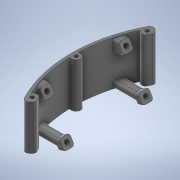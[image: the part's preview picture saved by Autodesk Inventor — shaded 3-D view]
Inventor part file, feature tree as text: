
AUTODESK INVENTOR PART (.ipt)
format: ipt  version: 2020 (Build 240168000, 168)  size: 1,327,616 bytes
history: native  units: mm
features: projected_geometry x30, extrude x17, sketch x12, other x9, fillet x1
ambient origin geometry x8: Origin, YZ Plane, XZ Plane, XY Plane, X Axis, Y Axis, Z Axis, Center Point
bodies: Body1 (feature_tree)
feature tree (69):
  other  "Твердое тело1"
  extrude  "outer"  TaperAngle=45.0deg  [1 undecoded]
  extrude  "inner"  Depth=7.0mm
  sketch  "Эскиз3"
  extrude  "Выдавливание3"  Depth=20.0mm
  extrude  "Выдавливание4"  Depth=7.0mm
  sketch  "Эскиз4"
  extrude  "Выдавливание5"  Depth=3.2mm
  extrude  "Выдавливание6"  Depth=59.0mm
  sketch  "Эскиз5"
  extrude  "Выдавливание7"  Depth=83.0mm
  extrude  "Выдавливание8"  Depth=69.0mm
  sketch  "Эскиз6"
  extrude  "Выдавливание9"  Depth=55.0mm
  extrude  "Выдавливание10"  Depth=3.0mm
  fillet  "Сопряжение1"  Radius=8.0mm
  other  "РабПлоскость2"
  other  "РабПлоскость3"
  sketch  "Эскиз10"
  sketch  "Эскиз11"
  other  "РабПлоскость4"
  other  "РабПлоскость5"
  other  "РабОсь2"
  other  "РабОсь1"
  sketch  "Эскиз12"
  extrude  "Выдавливание12"  Depth=5.0mm
  sketch  "Эскиз8"
  extrude  "asterisk"  Depth=2.0mm
  other  "РабПлоскость7"
  sketch  "Эскиз13"
  extrude  "Выдавливание13"  Depth=40.0mm TaperAngle=360.0deg
  extrude  "Выдавливание14"  Depth=2.0mm
  extrude  "Выдавливание15"  Depth=105.0mm
  extrude  "Выдавливание16"  Depth=2.0mm
  extrude  "Выдавливание17"  Depth=2.0mm TaperAngle=0.0deg
  sketch  "Эскиз1"
  sketch  "Эскиз2"
  projected_geometry  "Спроецированная петля1"
  projected_geometry  "Спроецированная петля2"
  projected_geometry  "Спроецированная петля3"
  projected_geometry  "Спроецированная петля4"
  projected_geometry  "Спроецированная петля5"
  projected_geometry  "Спроецированная петля8"
  projected_geometry  "Спроецированная петля9"
  projected_geometry  "Спроецированная петля10"
  projected_geometry  "Спроецированная петля11"
  projected_geometry  "Спроецированная петля12"
  other  "РабПлоскость6"
  projected_geometry  "Спроецированная петля13"
  projected_geometry  "Спроецированная петля14"
  projected_geometry  "Спроецированная петля15"
  projected_geometry  "Спроецированная петля16"
  projected_geometry  "Спроецированная петля17"
  projected_geometry  "Спроецированная петля18"
  projected_geometry  "Спроецированная петля19"
  projected_geometry  "Спроецированная петля20"
  projected_geometry  "Спроецированная петля21"
  projected_geometry  "Спроецированная петля22"
  projected_geometry  "Спроецированная петля23"
  projected_geometry  "Спроецированная петля24"
  projected_geometry  "Спроецированная петля25"
  projected_geometry  "Спроецированная петля26"
  projected_geometry  "Спроецированная петля27"
  projected_geometry  "Спроецированная петля28"
  projected_geometry  "Спроецированная петля29"
  projected_geometry  "Спроецированная петля30"
  projected_geometry  "Спроецированная петля31"
  projected_geometry  "Спроецированная петля32"
  sketch  "Эскиз14"
note: 1 required parameter value undecoded (feature->parameter linkage not recoverable at this tier; creation-order binding heuristic only, values carry confidence <= 0.55)
